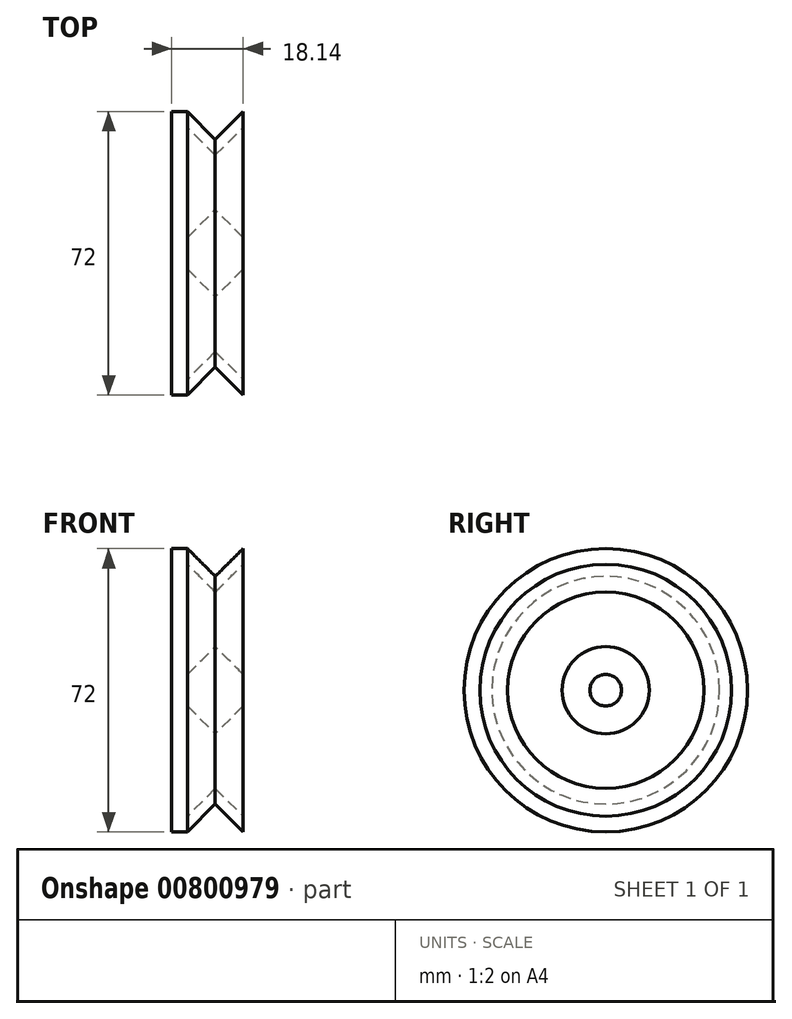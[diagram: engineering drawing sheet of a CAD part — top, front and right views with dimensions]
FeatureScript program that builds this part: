
annotation { "Feature Type Name" : "Feature", "Feature Type Description" : "" }
export const myFeature = defineFeature(function(context is Context, id is Id, definition is map)
    precondition{}
    {
        {
            var Q0;
            Q0=qCreatedBy(makeId("Top.planeOp"),FACE);
            var sketch = newSketch(context, id + "F0", { "sketchPlane" : qUnion([Q0])});
            skLineSegment(sketch, "E0", {"start": v(0, 0) * mm, "end": v(0, -36) * mm});
            skLineSegment(sketch, "E1", {"start": v(0, -36) * mm, "end": v(4, -36) * mm});
            skLineSegment(sketch, "E2", {"start": v(4, -36) * mm, "end": v(11.07, -28.93) * mm});
            skLineSegment(sketch, "E3", {"start": v(11.07, -28.93) * mm, "end": v(18.14, -36) * mm});
            skLineSegment(sketch, "E4", {"start": v(18.14, -36) * mm, "end": v(18.14, -32) * mm});
            skLineSegment(sketch, "E5", {"start": v(18.14, -32) * mm, "end": v(11.07, -24.93) * mm});
            skLineSegment(sketch, "E6", {"start": v(11.07, -24.93) * mm, "end": v(4, -32) * mm});
            skLineSegment(sketch, "E7", {"start": v(4, -32) * mm, "end": v(4, -4) * mm});
            skLineSegment(sketch, "E8", {"start": v(4, -4) * mm, "end": v(11.07, -11.07) * mm});
            skLineSegment(sketch, "E9", {"start": v(11.07, -11.07) * mm, "end": v(18.14, -4) * mm});
            skLineSegment(sketch, "E10", {"start": v(18.14, -4) * mm, "end": v(18.14, 0) * mm});
            skLineSegment(sketch, "E11", {"start": v(18.14, 0) * mm, "end": v(11.07, -7.07) * mm});
            skLineSegment(sketch, "E12", {"start": v(4, -32) * mm, "end": v(0, -32) * mm, "construction": true});
            skLineSegment(sketch, "E13", {"start": v(4, -32) * mm, "end": v(4, -36) * mm, "construction": true});
            skLineSegment(sketch, "E14", {"start": v(11.07, -28.93) * mm, "end": v(11.07, -24.93) * mm, "construction": true});
            skLineSegment(sketch, "E15", {"start": v(4, -4) * mm, "end": v(0, -4) * mm, "construction": true});
            skLineSegment(sketch, "E16", {"start": v(0, -4) * mm, "end": v(4, -4) * mm, "construction": true});
            skLineSegment(sketch, "E17", {"start": v(4, 0) * mm, "end": v(4, -4) * mm, "construction": true});
            skLineSegment(sketch, "E18", {"start": v(11.07, -7.07) * mm, "end": v(11.07, -11.07) * mm, "construction": true});
            skLineSegment(sketch, "E19", {"start": v(11.07, -7.07) * mm, "end": v(4, 0) * mm});
            skLineSegment(sketch, "E20", {"start": v(4, 0) * mm, "end": v(0, 0) * mm});
            skLineSegment(sketch, "E21", {"start": v(4, 0) * mm, "end": v(18.14, 0) * mm});
            skSolve(sketch);
        }
        {
            var Q0;
            Q0=makeQuery(id+"F0.imprint","IMPRINT",FACE,{"disambiguationData":[TD([[makeQuery(id+"F0.imprint","IMPRINT",EDGE,{"derivedFrom":sQuery(id+"F0.wireOp",EDGE,"E0")}),1.0]])]});
            var Q1;
            Q1=makeQuery(id+"F0.imprint","IMPRINT",FACE,{"disambiguationData":[TD([[makeQuery(id+"F0.imprint","IMPRINT",EDGE,{"derivedFrom":sQuery(id+"F0.wireOp",EDGE,"E11")}),-1.0]])]});
            var Q2;
            Q2=sQuery(id+"F0.wireOp",EDGE,"E21");
            revolve(context, id + "F1", {"surfaceOperationType" : NewSurfaceOperationType.NEW, "entities" : qUnion([Q0, Q1]), "axis" : qUnion([Q2]), "revolveType" : RevolveType.FULL});
        }
    });
